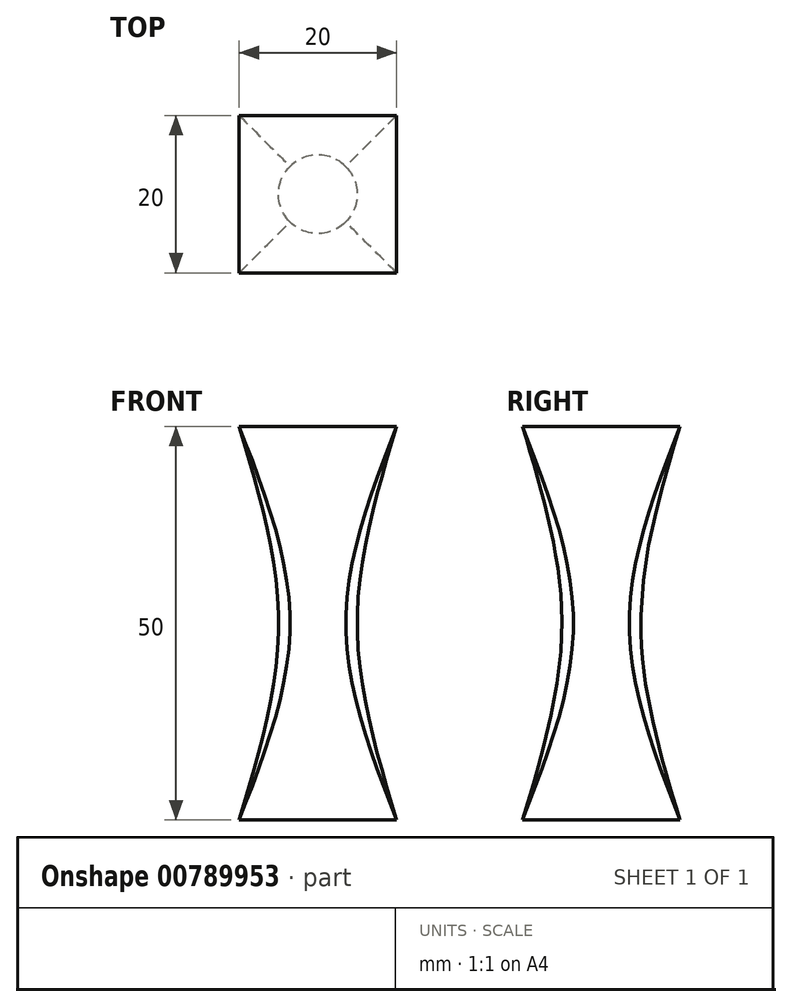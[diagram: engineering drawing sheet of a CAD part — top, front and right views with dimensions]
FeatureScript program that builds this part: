
annotation { "Feature Type Name" : "Feature", "Feature Type Description" : "" }
export const myFeature = defineFeature(function(context is Context, id is Id, definition is map)
    precondition{}
    {
        {
            var Q0;
            Q0=qCreatedBy(makeId("Top.planeOp"),FACE);
            var sketch = newSketch(context, id + "F0", { "sketchPlane" : qUnion([Q0])});
            skLineSegment(sketch, "E0.bottom", {"start": v(-10, 10) * mm, "end": v(10, 10) * mm});
            skLineSegment(sketch, "E0.top", {"start": v(-10, -10) * mm, "end": v(10, -10) * mm});
            skLineSegment(sketch, "E0.left", {"start": v(-10, 10) * mm, "end": v(-10, -10) * mm});
            skLineSegment(sketch, "E0.right", {"start": v(10, 10) * mm, "end": v(10, -10) * mm});
            skPoint(sketch, "E0.middle", {"position": v(0, 0) * mm});
            skSolve(sketch);
        }
        {
            var Q0;
            Q0=qCreatedBy(makeId("Top.planeOp"),FACE);
            cPlane(context, id + "F1", {"entities" : qUnion([Q0]), "cplaneType" : CPlaneType.OFFSET, "offset" : 25 * mm, "width" : 150 * mm, "height" : 150 * mm});
        }
        {
            var Q0;
            Q0=qCreatedBy(id+"F1.planeOp",FACE);
            var sketch = newSketch(context, id + "F2", { "sketchPlane" : qUnion([Q0])});
            skCircle(sketch, "E1", {"center": v(0, 0) * mm, "radius": 5 * mm});
            skSolve(sketch);
        }
        {
            var Q0;
            Q0=qCreatedBy(makeId("Top.planeOp"),FACE);
            cPlane(context, id + "F3", {"entities" : qUnion([Q0]), "cplaneType" : CPlaneType.OFFSET, "offset" : 50 * mm, "width" : 150 * mm, "height" : 150 * mm});
        }
        {
            var Q0;
            Q0=qCreatedBy(id+"F3.planeOp",FACE);
            var sketch = newSketch(context, id + "F4", { "sketchPlane" : qUnion([Q0])});
            skLineSegment(sketch, "E2.0.0", {"start": v(-10, 10) * mm, "end": v(-10, -10) * mm});
            skLineSegment(sketch, "E2.0.1", {"start": v(-10, -10) * mm, "end": v(10, -10) * mm});
            skLineSegment(sketch, "E2.0.2", {"start": v(10, -10) * mm, "end": v(10, 10) * mm});
            skLineSegment(sketch, "E2.0.3", {"start": v(10, 10) * mm, "end": v(-10, 10) * mm});
            skSolve(sketch);
        }
        {
            var Q0;
            Q0 = qSketchRegion(id + "F0", true);
            var Q1;
            Q1 = qSketchRegion(id + "F2", true);
            var Q2;
            Q2 = qSketchRegion(id + "F4", true);
            loft(context, id + "F5", {"sheetProfilesArray" : [{ "sheetProfileEntities" : qUnion([Q0]) }, { "sheetProfileEntities" : qUnion([Q1]) }, { "sheetProfileEntities" : qUnion([Q2]) }]});
        }
    });
